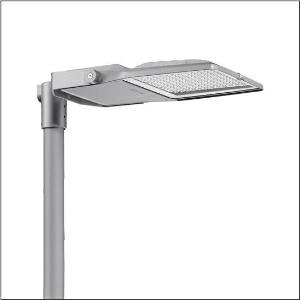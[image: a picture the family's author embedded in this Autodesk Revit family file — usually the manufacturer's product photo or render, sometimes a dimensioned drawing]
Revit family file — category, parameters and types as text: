
# Revit family: floodlight_fl_21_iq_midi___pl33t_5xa7781e6f3a_cd97
name_source: partatom
category: Lighting Fixtures
units: mm (PartAtom-declared; Revit-internal decimal feet)

## family parameters
Cut with Voids When Loaded = No
Host = Face
Light Source = No
Part Type = Normal
Room Calculation Point = No
Round Connector Dimension = Use Diameter
Shared = No

## types (1)
- --- (1 x LED, 21270 lm, 208.1 W, 5700K)
    Apparent Load = 208 VA
    CIE Flux Codes = 26 75 99 100 100
    Color Rendering = 90
    Color Temperature = 5700K
    Default Elevation = 1800 mm
    Description = Floodlight FL 21 iQ midi, floodlight, primary light control with lens, of PMMA, primary optical cover: protective disc, of toughened safety glass, transparent, light distribution: PL33T, light emission: direct distribution, installation type: surface-mounted, LED, High Power LED, rated luminous flux: 21.270lm, luminous efficacy: 102lm/W, light colour: 957, colour temperature: 5700K, control gear: ECG iQ, control: optimised constant luminous flux control (CLO 2.0), Desk-Remote (wireless, voltage-free reading and setting of iQ features in the workshop via application-optimized NFC function/RFID function), Light-Fading, Smart-Wire, Night-Set, Lumen-Switch, Temp-Guard, Auto-Match, with terminal, 6-pole, mains connection: 220..240V, AC, 50/60Hz, start of lifetime: 208W, end of service life: 227W, reduction: 90W, luminaire housing, of diecast aluminium, powder-coated, Siteco® metallic grey (DB 702S), corrosivity category C5 mid according to DIN EN ISO 12944, sealing non-destructively replaceable, please order mast flange separately, mast bracket, of steel, galvanised, powder-coated, Siteco® metallic grey (DB 702S), protection rating (complete): IP66, insulation class (complete): insulation class II (safety insulation), certification: CE, protection symbol: D, impact resistance: IK08, permissible operating ambient temperature: -40..+40°C, permissible operating ambient temperature for outdoor applications: -40..+50°C, standard: DIN EN 12944, LABS conformity tested according to VDMA 24364:2018-05, packaging unit: 1 piece

Light Distribution: PL33T
    Height = 76 mm
    Lamp = 1 x LED
    Lamp Light Flux = 21270 lm
    Lamp Power = 208.1 W
    Lamp count = 1
    Length = 657 mm
    Luminous efficacy = 102 lm/W
    Manufacturer = Siteco
    ModVariant = No
    Model = 5XA7781E6F3A
    Number of Poles = 1
    OnlyDefault = Yes
    Power Factor = 1
    Product Name = Floodlight FL 21 iQ midi | PL33T
    Product group = floodlight | pylon annexe
    ProductGroupID = 6200
    Protection Class = Protection class II
    Protection Degree = IP 66
    RLX_Detail_Level = 1
    RLX_Emergency_Light_Flux = 0 lm
    RLX_Emergency_Type = 0
    RLX_Emergency_Type_DB = No
    RlxData = <blob elided: 153685 chars, md5=fd85fa74>
    Socket = socket
    Standby Power = 0 W
    System Light Flux = 21270 lm
    System Power = 208 W
    Type Comments = factory setting: luminous flux: 100 % | dim-lin: 254 | 710 mA
    Type Image = l_1007123.jpg
    URL = http://relux.com
    VarID = @adj_051925
    Voltage = 0 V
    Weight = 0.00 kg
    Width = 442 mm

## geometry (parser evidence)
native form markers: Blend x4, Sweep x11
no freeform markers — native parametric forms only
